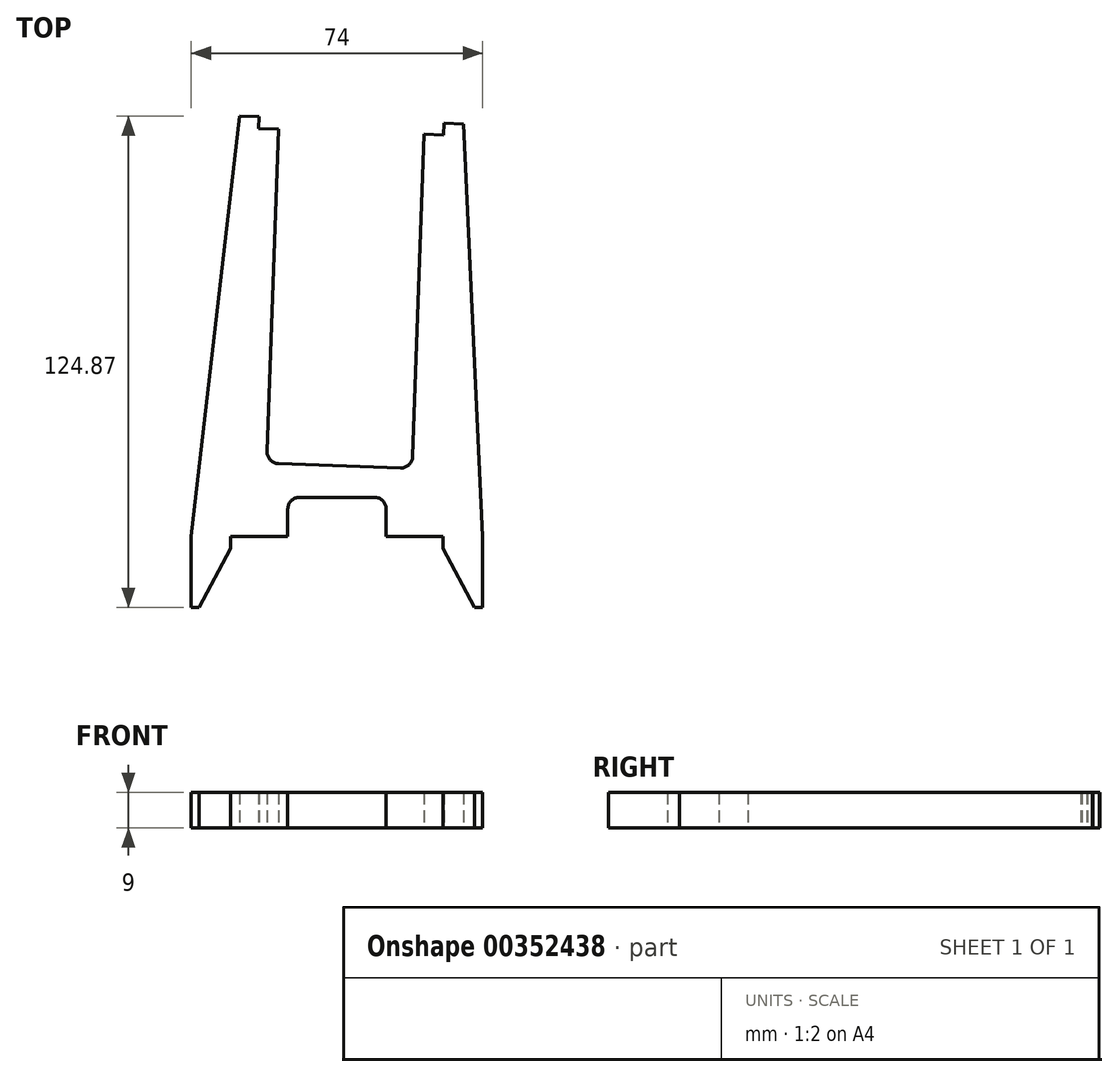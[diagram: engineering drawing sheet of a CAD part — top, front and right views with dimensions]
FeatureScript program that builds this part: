
annotation { "Feature Type Name" : "Feature", "Feature Type Description" : "" }
export const myFeature = defineFeature(function(context is Context, id is Id, definition is map)
    precondition{}
    {
        {
            var Q0;
            Q0=qCreatedBy(makeId("Top.planeOp"),FACE);
            var sketch = newSketch(context, id + "F0", { "sketchPlane" : qUnion([Q0])});
            skLineSegment(sketch, "E0", {"start": v(-27, 0) * mm, "end": v(-12.5, 0) * mm});
            skLineSegment(sketch, "E1", {"start": v(37, 0) * mm, "end": v(32.18, 104.88) * mm});
            skLineSegment(sketch, "E2", {"start": v(-24.79, 106.87) * mm, "end": v(-37, 0) * mm});
            skLineSegment(sketch, "E3", {"start": v(0, 0) * mm, "end": v(3.7, 106) * mm, "construction": true});
            skLineSegment(sketch, "E4", {"start": v(22.08, 102.23) * mm, "end": v(19.22, 20.35) * mm});
            skLineSegment(sketch, "E5", {"start": v(16.12, 17.46) * mm, "end": v(-14.86, 18.54) * mm});
            skLineSegment(sketch, "E6", {"start": v(-17.76, 21.64) * mm, "end": v(-14.9, 103.52) * mm});
            skPoint(sketch, "E7", {"position": v(0.63, 18) * mm});
            skLineSegment(sketch, "E8.right", {"start": v(-12.5, 7) * mm, "end": v(-12.5, 0) * mm});
            skPoint(sketch, "E8.middle", {"position": v(0, 0) * mm});
            skLineSegment(sketch, "E9.trimOffspring", {"start": v(12.5, 0) * mm, "end": v(27, 0) * mm});
            skLineSegment(sketch, "E10.MirrorCS", {"start": v(12.5, 7) * mm, "end": v(12.5, 0) * mm});
            skLineSegment(sketch, "E11", {"start": v(-9.5, 10) * mm, "end": v(9.5, 10) * mm});
            skPoint(sketch, "E12.MirrorCS.start.orphan", {"position": v(37, 0) * mm});
            skLineSegment(sketch, "E13", {"start": v(-19.79, 106.7) * mm, "end": v(-19.9, 103.7) * mm});
            skPoint(sketch, "E14.orphan", {"position": v(-24.79, 106.87) * mm});
            skLineSegment(sketch, "E15", {"start": v(27.18, 105.05) * mm, "end": v(27.08, 102.05) * mm});
            skPoint(sketch, "E16.orphan", {"position": v(32.18, 104.88) * mm});
            skLineSegment(sketch, "E17", {"start": v(-24.79, 106.87) * mm, "end": v(-19.79, 106.7) * mm});
            skLineSegment(sketch, "E18", {"start": v(-19.9, 103.7) * mm, "end": v(-14.9, 103.52) * mm});
            skLineSegment(sketch, "E19", {"start": v(27.18, 105.05) * mm, "end": v(32.18, 104.88) * mm});
            skLineSegment(sketch, "E20", {"start": v(27.08, 102.05) * mm, "end": v(22.08, 102.23) * mm});
            skPoint(sketch, "E21.orphan", {"position": v(-37.03, -21.75) * mm});
            skPoint(sketch, "E22.visualSharp", {"position": v(19.12, 17.35) * mm});
            skArc(sketch, "E22.filletArc", {"start": v(16.12, 17.46) * mm, "mid": v(18.27, 18.26) * mm, "end": v(19.22, 20.35) * mm});
            skPoint(sketch, "E23.visualSharp", {"position": v(-17.86, 18.65) * mm});
            skArc(sketch, "E23.filletArc", {"start": v(-17.76, 21.64) * mm, "mid": v(-16.95, 19.5) * mm, "end": v(-14.86, 18.54) * mm});
            skPoint(sketch, "E24.visualSharp", {"position": v(-12.5, 10) * mm});
            skArc(sketch, "E24.filletArc", {"start": v(-9.5, 10) * mm, "mid": v(-11.62, 9.12) * mm, "end": v(-12.5, 7) * mm});
            skPoint(sketch, "E25.visualSharp", {"position": v(12.5, 10) * mm});
            skArc(sketch, "E25.filletArc", {"start": v(12.5, 7) * mm, "mid": v(11.62, 9.12) * mm, "end": v(9.5, 10) * mm});
            skLineSegment(sketch, "E26", {"start": v(-37, 0) * mm, "end": v(-37, 0) * mm});
            skLineSegment(sketch, "E27", {"start": v(-37, 0) * mm, "end": v(-37, -18) * mm});
            skLineSegment(sketch, "E28", {"start": v(-37, -18) * mm, "end": v(-35, -18) * mm});
            skLineSegment(sketch, "E29", {"start": v(-27, 0) * mm, "end": v(-27, -3) * mm});
            skLineSegment(sketch, "E30", {"start": v(-27, -3) * mm, "end": v(-35, -18) * mm});
            skLineSegment(sketch, "E31.MirrorCS", {"start": v(27, 0) * mm, "end": v(27, -3) * mm});
            skLineSegment(sketch, "E32.MirrorCS", {"start": v(27, -3) * mm, "end": v(35, -18) * mm});
            skLineSegment(sketch, "E33.MirrorCS", {"start": v(37, -18) * mm, "end": v(35, -18) * mm});
            skLineSegment(sketch, "E34.MirrorCS", {"start": v(37, 0) * mm, "end": v(37, -18) * mm});
            skLineSegment(sketch, "E35.MirrorCS", {"start": v(37, 0) * mm, "end": v(37, 0) * mm});
            skSolve(sketch);
        }
        {
            var Q0;
            Q0=makeQuery(id+"F0.imprint","IMPRINT",FACE,{"disambiguationData":[TD([[makeQuery(id+"F0.imprint","IMPRINT",EDGE,{"derivedFrom":sQuery(id+"F0.wireOp",EDGE,"E0")}),1.0]])]});
            extrude(context, id + "F1", {"entities" : qUnion([Q0]), "depth" : 9 * mm, "symmetric" : true});
        }
    });
